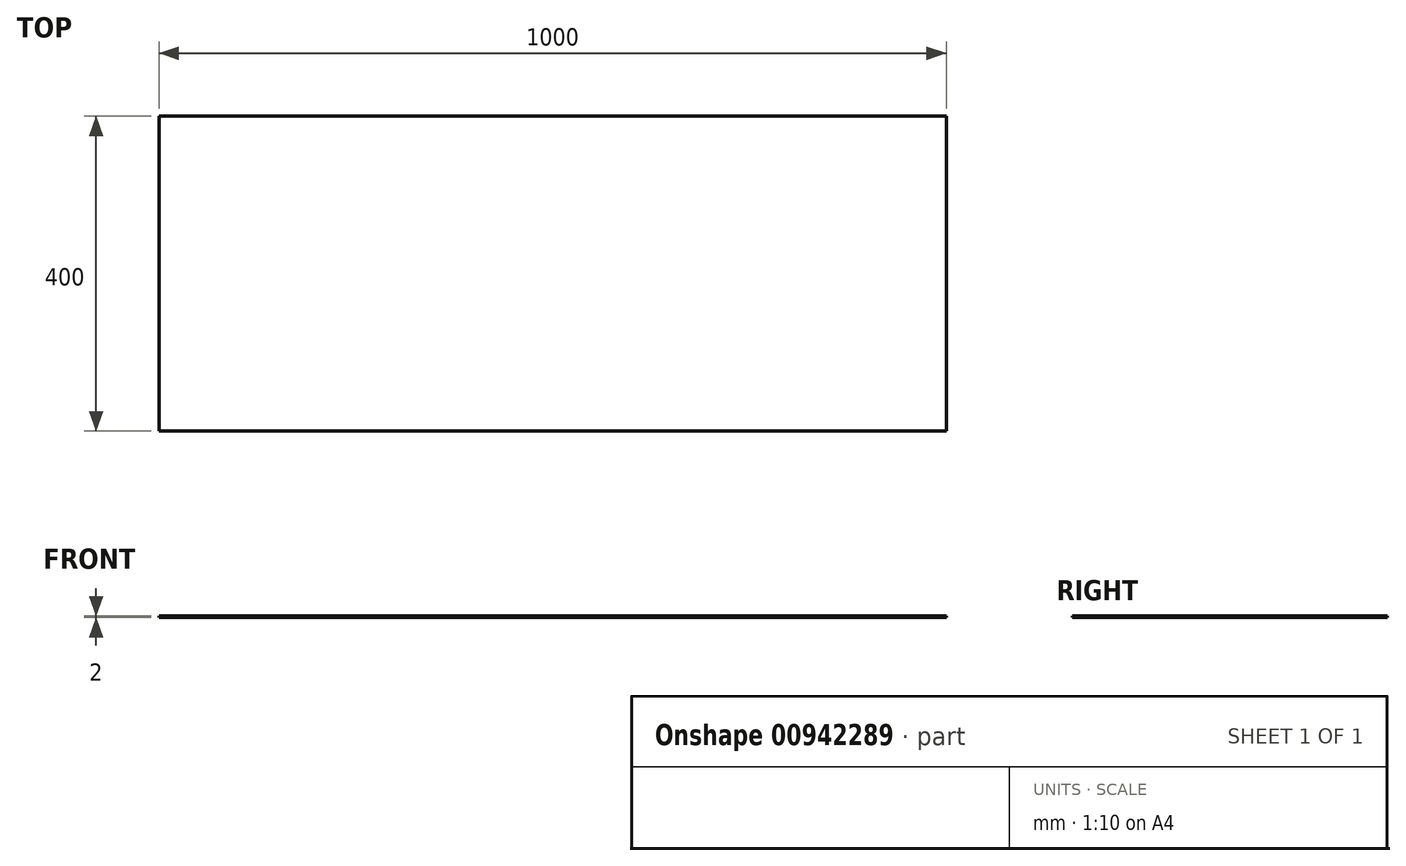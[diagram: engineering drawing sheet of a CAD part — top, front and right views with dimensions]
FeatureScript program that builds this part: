
annotation { "Feature Type Name" : "Feature", "Feature Type Description" : "" }
export const myFeature = defineFeature(function(context is Context, id is Id, definition is map)
    precondition{}
    {
        {
            var Q0;
            Q0=qCreatedBy(makeId("Top.planeOp"),FACE);
            var sketch = newSketch(context, id + "F0", { "sketchPlane" : qUnion([Q0])});
            skLineSegment(sketch, "E0.bottom", {"start": v(0, 0) * mm, "end": v(1000, 0) * mm});
            skLineSegment(sketch, "E0.top", {"start": v(0, 400) * mm, "end": v(1000, 400) * mm});
            skLineSegment(sketch, "E0.left", {"start": v(0, 0) * mm, "end": v(0, 400) * mm});
            skLineSegment(sketch, "E0.right", {"start": v(1000, 0) * mm, "end": v(1000, 400) * mm});
            skSolve(sketch);
        }
        {
            var Q0;
            Q0 = qSketchRegion(id + "F0", true);
            extrude(context, id + "F1", {"entities" : qUnion([Q0]), "depth" : 2 * mm, "offsetDistance" : 25 * mm});
        }
    });
